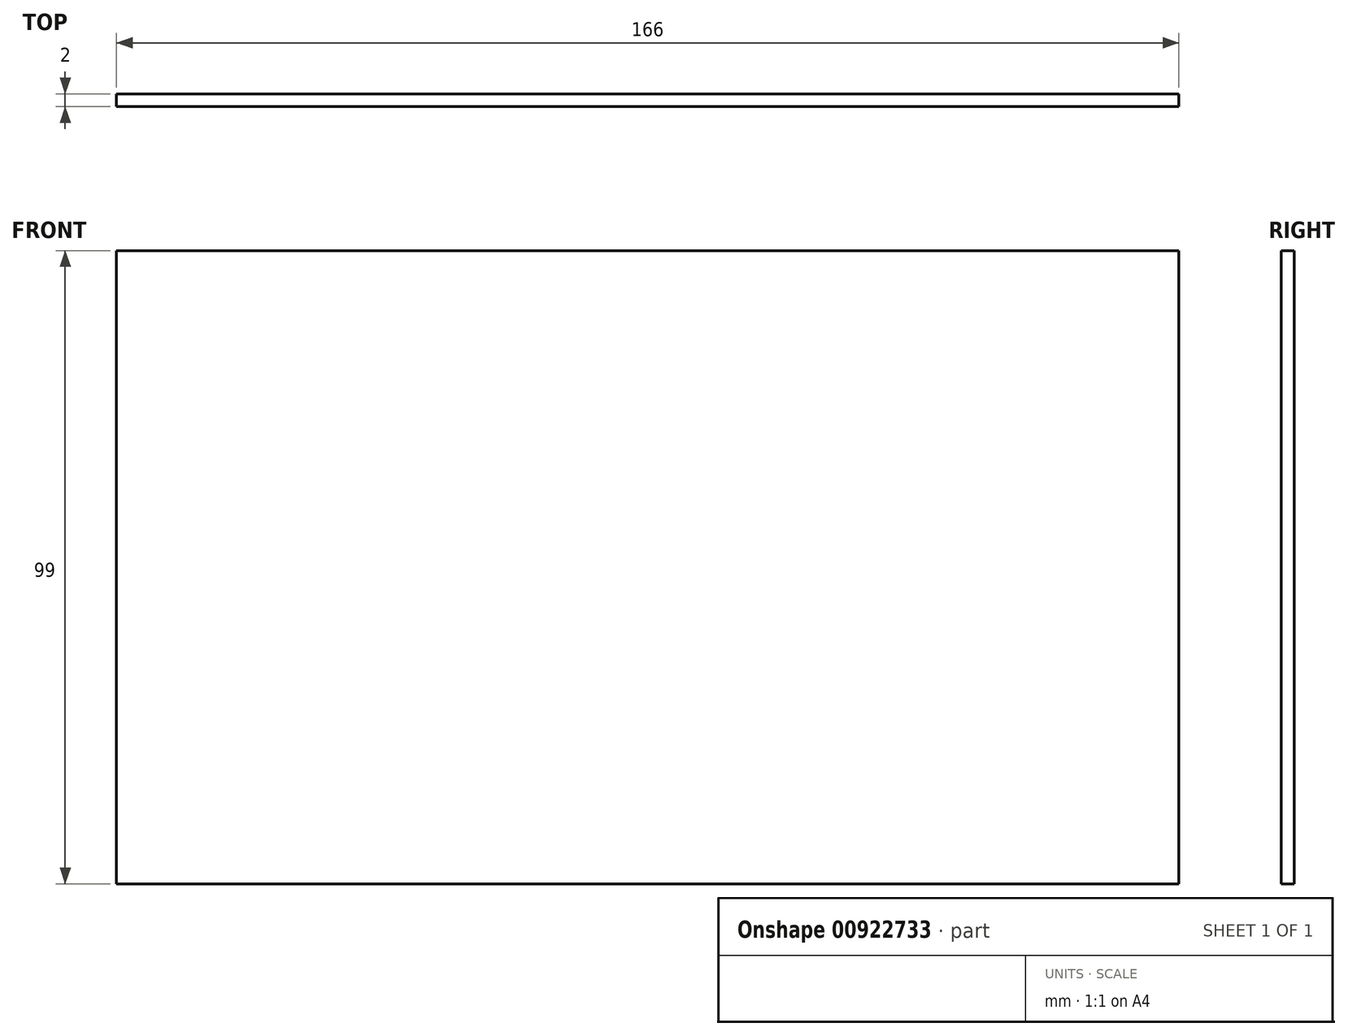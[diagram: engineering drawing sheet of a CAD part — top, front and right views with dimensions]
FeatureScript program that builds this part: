
annotation { "Feature Type Name" : "Feature", "Feature Type Description" : "" }
export const myFeature = defineFeature(function(context is Context, id is Id, definition is map)
    precondition{}
    {
        {
            var Q0;
            Q0=qCreatedBy(makeId("Front.planeOp"),FACE);
            var sketch = newSketch(context, id + "F0", { "sketchPlane" : qUnion([Q0])});
            skLineSegment(sketch, "E0.bottom", {"start": v(83, -49.5) * mm, "end": v(-83, -49.5) * mm});
            skLineSegment(sketch, "E0.top", {"start": v(83, 49.5) * mm, "end": v(-83, 49.5) * mm});
            skLineSegment(sketch, "E0.left", {"start": v(83, -49.5) * mm, "end": v(83, 49.5) * mm});
            skLineSegment(sketch, "E0.right", {"start": v(-83, -49.5) * mm, "end": v(-83, 49.5) * mm});
            skPoint(sketch, "E0.middle", {"position": v(0, 0) * mm});
            skSolve(sketch);
        }
        {
            var Q0;
            Q0 = qSketchRegion(id + "F0", true);
            extrude(context, id + "F1", {"entities" : qUnion([Q0]), "endBound" : BoundingType.SYMMETRIC, "depth" : 2 * mm, "offsetDistance" : 25 * mm});
        }
    });
